# Revit family: Deca_Cuba quadrada de apoio com mesa_Quadratta_L.11040.M
name_source: partatom
category: Plumbing Fixtures
units: mm (PartAtom-declared; Revit-internal decimal feet)

## family parameters
Cut with Voids When Loaded = Yes
Host = Face
Part Type = Normal
Room Calculation Point = No
Round Connector Dimension = Use Radius
Shared = No

## types (3) — shared parameters
Acompanha o Produto = Retentor Válvula 7701165 ; Folheto cuba squarcle 7920265 ; Tampão Cerâmico para válvula de cozinha (v.15.17.cla);
Aprovado por = quattroD
Atendimento ao Cliente = 0800-0117073
Categoria = Cubas
Composição Anel Vedação = -
Composição Assento = -
Composição Básica = Argila; feldspato; caulim; vidrados e corantes inorgânicos.
Composição Componente = Aço inoxidável; elastômeros e plásticos de engenharia.
Consumo = -
Cor Secundária = -
Cores Componente = -
Criado por = quattroD
Código Pai = L.11040.M
Diâmetro Ponto de Esgoto = 0.03 m
Informações Complementares = -
Itens de Instalação = -
Linha = Quadratta
Manufacturer = Deca
Norma = NBR-16728-1;NBR-16728-2
Pressão máx. funcionamento = -
Pressão mín. Aquec. Acúmulo = -
Pressão mín. Aquec. Passagem = -
Pressão mín. funcionamento = -
Raio Ponto de Esgoto = 0.01 m
Segmento = Banheiro Luxo
Tipo de dispositivo economizador = -
Tipo de mecanismo utilizado = -
Tipo de rosca de entrada = -
Tipo de rosca de saída = -
URL = www.deca.com.br
Vazão na Pressão máx. (L/min) = -
Vazão na Pressão mín. (L/min) = -
zero-valued in all types: Default Elevation

## per-type parameters (varying)
| type | Cor Interna | Cor Principal | Description | Material | Model | Peso Líquido (Kg) | Saída de Esgoto |
| L.11040.M.17_Branco | 17 - Branco | 17 - Branco | CUBA QUADRADA DE APOIO COM MESA 40 CM - BRANCA | Deca_Branco | L.11040.M.17 | 12079 | Válvula Curta |
| L.11040.M.22_Marrom Fosco | 22 - Marrom Fosco | 22 - Marrom Fosco | CUBA QUADRADA DE APOIO COM MESA 40 CM - MARROM FOSCO | Deca_Marrom Fosco | L.11040.M.22 | 11822 | Válvula Curta |
| L.11040.M.94_Ébano Fosco | 94 - Ébano Fosco | 94 - Ébano Fosco | CUBA QUADRADA DE APOIO COM MESA 40 CM - ÉBANO FOSCO | Deca_Ébano Fosco | L.11040.M.94 | 11822 | Válvula Oculta |

## geometry (parser evidence)
native form markers: Sweep x3
no freeform markers — native parametric forms only
